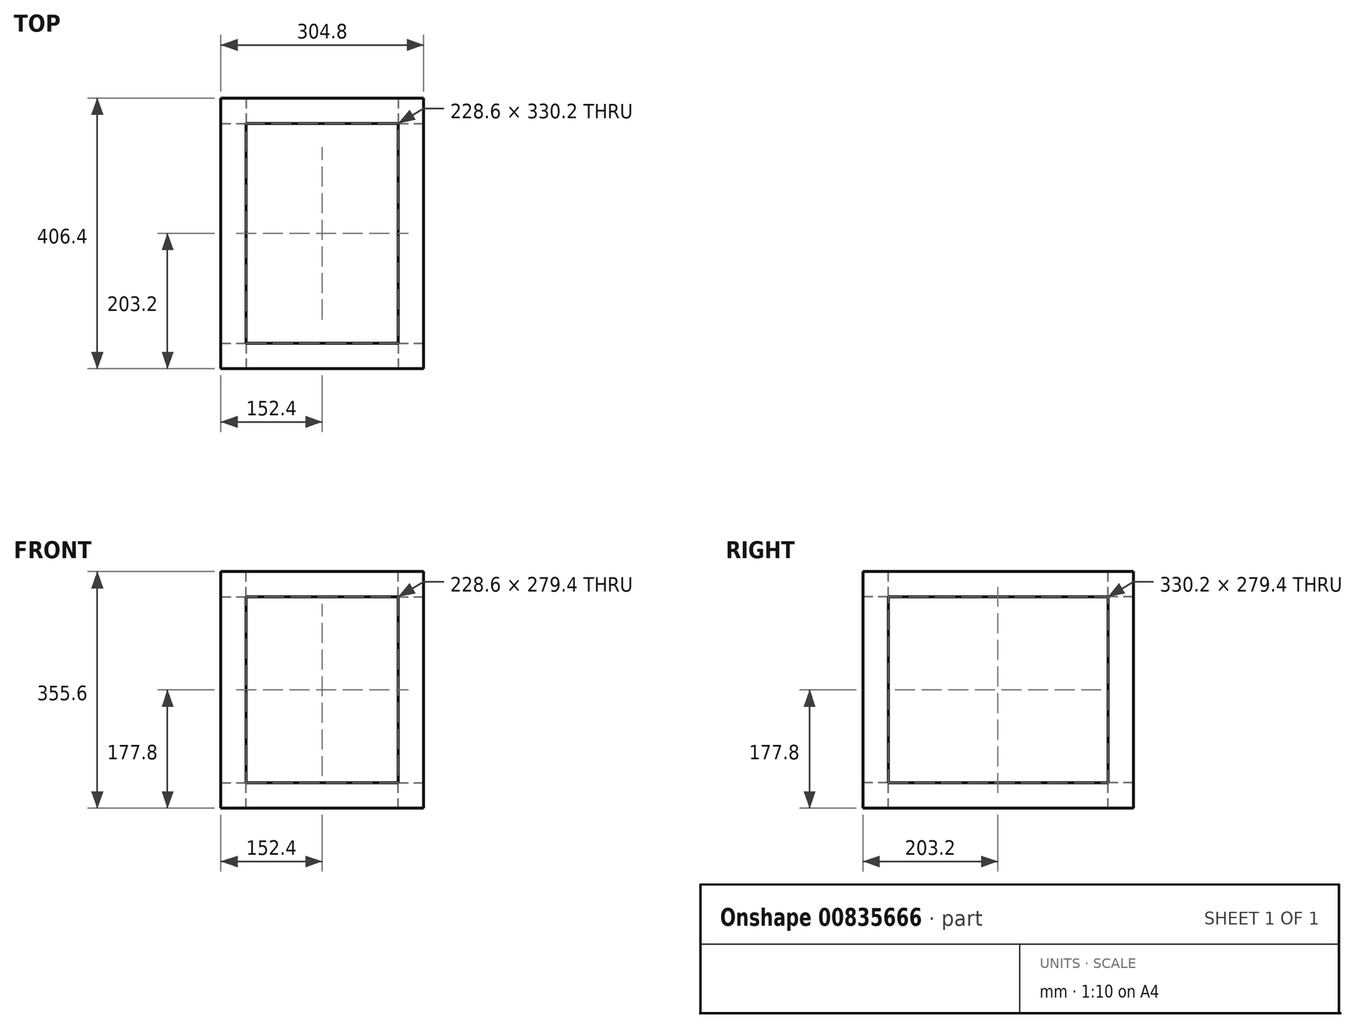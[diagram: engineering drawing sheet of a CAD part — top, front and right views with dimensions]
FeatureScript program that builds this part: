
annotation { "Feature Type Name" : "Feature", "Feature Type Description" : "" }
export const myFeature = defineFeature(function(context is Context, id is Id, definition is map)
    precondition{}
    {
        {
            var Q0;
            Q0=qCreatedBy(makeId("Top.planeOp"),FACE);
            var sketch = newSketch(context, id + "F0", { "sketchPlane" : qUnion([Q0])});
            skLineSegment(sketch, "E0.bottom", {"start": v(-152.4, 203.2) * mm, "end": v(152.4, 203.2) * mm});
            skLineSegment(sketch, "E0.top", {"start": v(-152.4, -203.2) * mm, "end": v(152.4, -203.2) * mm});
            skLineSegment(sketch, "E0.left", {"start": v(-152.4, 203.2) * mm, "end": v(-152.4, -203.2) * mm});
            skLineSegment(sketch, "E0.right", {"start": v(152.4, 203.2) * mm, "end": v(152.4, -203.2) * mm});
            skLineSegment(sketch, "E1", {"start": v(-152.4, 203.2) * mm, "end": v(152.4, -203.2) * mm, "construction": true});
            skSolve(sketch);
        }
        {
            var Q0;
            Q0=makeQuery(id+"F0.imprint","IMPRINT",FACE,{"disambiguationData":[TD([[makeQuery(id+"F0.imprint","IMPRINT",EDGE,{"derivedFrom":sQuery(id+"F0.wireOp",EDGE,"E0.bottom")}),-1.0]])]});
            extrude(context, id + "F1", {"entities" : qUnion([Q0]), "endBound" : BoundingType.SYMMETRIC, "depth" : 355.6 * mm, "offsetDistance" : 25.4 * mm});
        }
        {
            var Q0;
            Q0=qCreatedBy(makeId("Front.planeOp"),FACE);
            var sketch = newSketch(context, id + "F2", { "sketchPlane" : qUnion([Q0])});
            skLineSegment(sketch, "E2.bottom", {"start": v(-114.3, 139.7) * mm, "end": v(114.3, 139.7) * mm});
            skLineSegment(sketch, "E2.top", {"start": v(-114.3, -139.7) * mm, "end": v(114.3, -139.7) * mm});
            skLineSegment(sketch, "E2.left", {"start": v(-114.3, 139.7) * mm, "end": v(-114.3, -139.7) * mm});
            skLineSegment(sketch, "E2.right", {"start": v(114.3, 139.7) * mm, "end": v(114.3, -139.7) * mm});
            skLineSegment(sketch, "E3", {"start": v(114.3, -139.7) * mm, "end": v(-114.3, 139.7) * mm, "construction": true});
            skSolve(sketch);
        }
        {
            var Q0;
            Q0 = qSketchRegion(id + "F2", true);
            extrude(context, id + "F3", {"entities" : qUnion([Q0]), "operationType" : NewBodyOperationType.REMOVE, "endBound" : BoundingType.SYMMETRIC, "oppositeDirection" : true, "depth" : 508 * mm, "offsetDistance" : 25.4 * mm});
        }
        {
            var Q0;
            Q0=qCreatedBy(makeId("Right.planeOp"),FACE);
            var sketch = newSketch(context, id + "F4", { "sketchPlane" : qUnion([Q0])});
            skLineSegment(sketch, "E4.bottom", {"start": v(-165.1, 139.7) * mm, "end": v(165.1, 139.7) * mm});
            skLineSegment(sketch, "E4.top", {"start": v(-165.1, -139.7) * mm, "end": v(165.1, -139.7) * mm});
            skLineSegment(sketch, "E4.left", {"start": v(-165.1, 139.7) * mm, "end": v(-165.1, -139.7) * mm});
            skLineSegment(sketch, "E4.right", {"start": v(165.1, 139.7) * mm, "end": v(165.1, -139.7) * mm});
            skLineSegment(sketch, "E5", {"start": v(-165.1, 139.7) * mm, "end": v(165.1, -139.7) * mm, "construction": true});
            skSolve(sketch);
        }
        {
            var Q0;
            Q0 = qSketchRegion(id + "F4", true);
            extrude(context, id + "F5", {"entities" : qUnion([Q0]), "operationType" : NewBodyOperationType.REMOVE, "endBound" : BoundingType.SYMMETRIC, "oppositeDirection" : true, "depth" : 508 * mm, "offsetDistance" : 25.4 * mm});
        }
        {
            var Q0;
            Q0=qCreatedBy(makeId("Top.planeOp"),FACE);
            var sketch = newSketch(context, id + "F6", { "sketchPlane" : qUnion([Q0])});
            skLineSegment(sketch, "E6.bottom", {"start": v(-114.3, 165.1) * mm, "end": v(114.3, 165.1) * mm});
            skLineSegment(sketch, "E6.top", {"start": v(-114.3, -165.1) * mm, "end": v(114.3, -165.1) * mm});
            skLineSegment(sketch, "E6.left", {"start": v(-114.3, 165.1) * mm, "end": v(-114.3, -165.1) * mm});
            skLineSegment(sketch, "E6.right", {"start": v(114.3, 165.1) * mm, "end": v(114.3, -165.1) * mm});
            skLineSegment(sketch, "E7", {"start": v(-114.3, 165.1) * mm, "end": v(114.3, -165.1) * mm, "construction": true});
            skSolve(sketch);
        }
        {
            var Q0;
            Q0 = qSketchRegion(id + "F6", true);
            extrude(context, id + "F7", {"entities" : qUnion([Q0]), "operationType" : NewBodyOperationType.REMOVE, "endBound" : BoundingType.SYMMETRIC, "oppositeDirection" : true, "depth" : 508 * mm, "offsetDistance" : 25.4 * mm});
        }
    });
